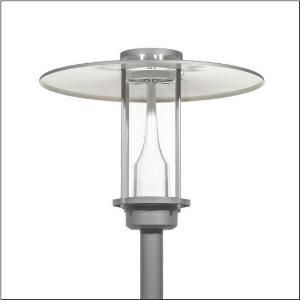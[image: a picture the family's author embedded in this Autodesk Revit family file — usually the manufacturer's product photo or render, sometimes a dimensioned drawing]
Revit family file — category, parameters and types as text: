
# Revit family: city-light_plus_iq___p1_0a_5xa5275nf14hp_e05b
name_source: partatom
category: Lighting Fixtures
units: mm (PartAtom-declared; Revit-internal decimal feet)

## family parameters
Cut with Voids When Loaded = No
Host = Face
Light Source = No
Part Type = Normal
Room Calculation Point = No
Round Connector Dimension = Use Diameter
Shared = No

## types (1)
- --- (1 x LED, 4020 lm, 33.6 W, 2700K)
    Apparent Load = 34 VA
    CIE Flux Codes = 30 60 90 96 100
    Color Rendering = 70
    Color Temperature = 2700K
    Default Elevation = 1800 mm
    Description = City-Light Plus iQ, mast luminaire, Module 540 iQ-SR, primary light control with 3 zone facetted reflector, of plastic, silver coated, highly specular, structured, primary optical cover: cover, of PMMA, transparent, light distribution: P1.0a, light emission: direct distribution, primary light characteristic: strongly asymmetric, installation type: post-top, LED, High Power LED, rated luminous flux: 4.020lm, luminous efficacy: 120lm/W, light colour: 727, colour temperature: 2700K, control gear: iQ Street-Remote, control: pre-setting: logarithmic dimming characteristic, Street-Remote, Auto-Match, Temp-Guard, Lumen-Switch, Night-Set, Smart-Wire, Light-Fading, Desk-Remote (wireless, voltage-free reading and setting of iQ features in the workshop via application-optimized NFC function/RFID function), optimised constant luminous flux control (CLO 2.0), with terminal, 6-pole, max. 2.5mm², mains connection: 230..240V, AC, 50/60Hz, start of lifetime: 34W, end of service life: 36W, reduction: 15W, luminaire housing, upper part, of glass-fibre reinforced polyester, coated, Siteco® metallic grey (DB 702S), diameter: 750mm, height: 590mm, spigot size: d x l = 76 x 70mm (post-top) | with reducer (optional accessory) 60 x 70mm, mounting height: 3..5m, post-top mast mounting element, of diecast aluminium, coated, Siteco® metallic grey (DB 702S), Module 540 iQ-SR, traffic white (RAL 9016), equipment: Power, protection rating (complete): IP65, insulation class (complete): insulation class II (safety insulation), certification: CE, ENEC, VDE, packaging unit: 1 piece

Light Distribution: P1.0a
    Height = 590 mm
    Lamp = 1 x LED
    Lamp Light Flux = 4020 lm
    Lamp Power = 33.6 W
    Lamp count = 1
    Length = 750 mm
    Luminous efficacy = 120 lm/W
    Manufacturer = Siteco
    ModVariant = No
    Model = 5XA5275NF14HP
    Mounting Place = Pole
    Mounting Type = Pole top
    Number of Poles = 1
    OnlyDefault = Yes
    Power Factor = 1
    Product Name = City-Light Plus iQ | P1.0a
    Product group = mast luminaire | pylon top
    ProductGroupID = 6100
    Protection Class = Protection class II
    Protection Degree = IP 65
    RLX_Detail_Level = 1
    RLX_Emergency_Light_Flux = 0 lm
    RLX_Emergency_Type = 0
    RLX_Emergency_Type_DB = No
    RlxData = <blob elided: 52745 chars, md5=998cf2dd>
    Socket = socket
    Standby Power = 0 W
    System Light Flux = 4020 lm
    System Power = 34 W
    Type Comments = factory setting: luminous flux: 100 % | dim-lin: 254 | 695 mA
    Type Image = l_1006456.jpg
    URL = http://relux.com
    VarID = @adj_153855
    Voltage = 0 V
    Weight = 0.00 kg
    Width = 0 mm  [stored 0 ft]

note: [stored X ft] marks values corroborated as IEEE doubles in the binary element streams (Revit-internal decimal feet)

## geometry (parser evidence)
native form markers: Blend x4, Sweep x13
no freeform markers — native parametric forms only
